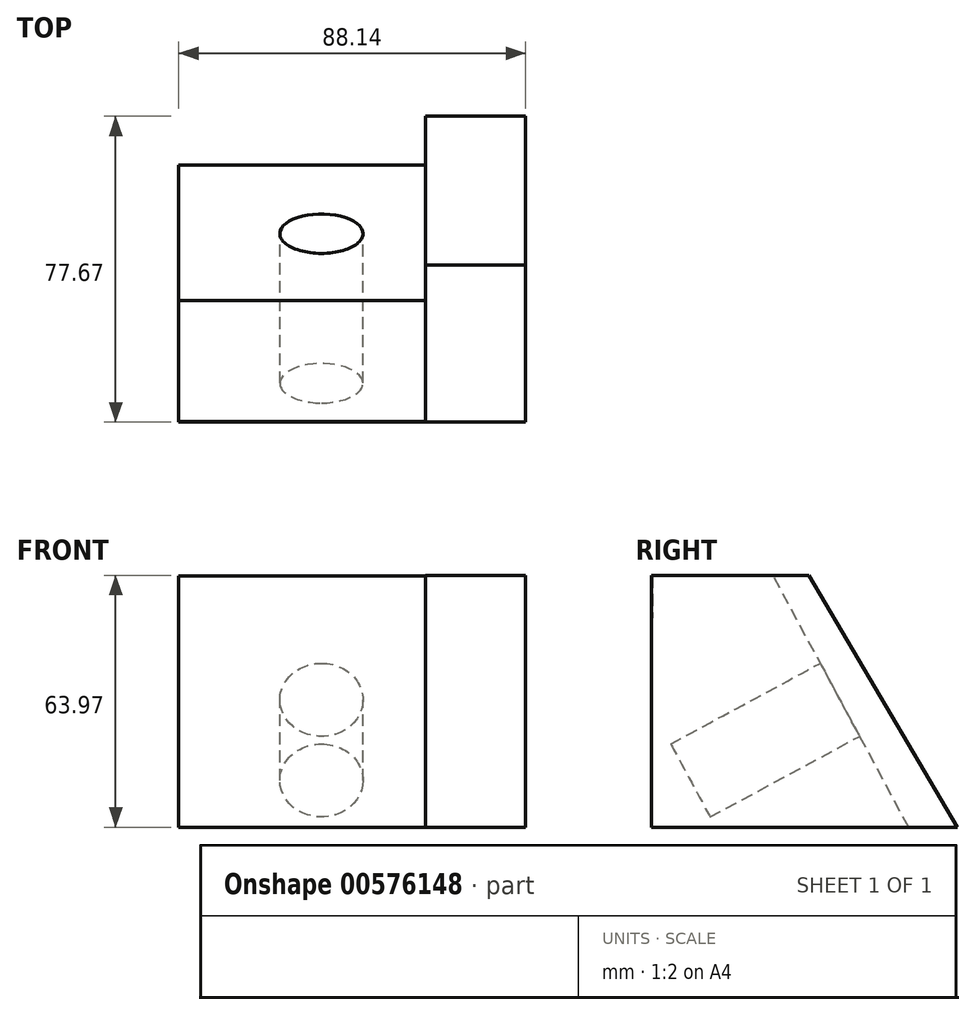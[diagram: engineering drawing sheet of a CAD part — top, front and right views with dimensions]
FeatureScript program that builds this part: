
annotation { "Feature Type Name" : "Feature", "Feature Type Description" : "" }
export const myFeature = defineFeature(function(context is Context, id is Id, definition is map)
    precondition{}
    {
        {
            var Q0;
            Q0=qCreatedBy(makeId("Right.planeOp"),FACE);
            var sketch = newSketch(context, id + "F0", { "sketchPlane" : qUnion([Q0])});
            skLineSegment(sketch, "E0.bottom", {"start": v(0, 0) * mm, "end": v(-39.92, 0) * mm});
            skLineSegment(sketch, "E0.top", {"start": v(0, 63.97) * mm, "end": v(-39.92, 63.97) * mm});
            skLineSegment(sketch, "E0.left", {"start": v(0, 0) * mm, "end": v(0, 63.97) * mm});
            skLineSegment(sketch, "E0.right", {"start": v(-39.92, 0) * mm, "end": v(-39.92, 63.97) * mm});
            skLineSegment(sketch, "E1", {"start": v(0, 63.97) * mm, "end": v(37.75, 0) * mm});
            skLineSegment(sketch, "E2", {"start": v(37.75, 0) * mm, "end": v(0, 0) * mm});
            skSolve(sketch);
        }
        {
            var Q0;
            Q0 = qSketchRegion(id + "F0", true);
            extrude(context, id + "F1", {"entities" : qUnion([Q0]), "depth" : 25.4 * mm, "offsetDistance" : 25.4 * mm});
        }
        {
            var Q0;
            Q0=qCreatedBy(makeId("Right.planeOp"),FACE);
            var sketch = newSketch(context, id + "F2", { "sketchPlane" : qUnion([Q0])});
            skLineSegment(sketch, "E3", {"start": v(-39.92, 0) * mm, "end": v(25.39, 0) * mm});
            skLineSegment(sketch, "E4", {"start": v(25.39, 0) * mm, "end": v(-9.02, 63.8) * mm});
            skLineSegment(sketch, "E5", {"start": v(-9.02, 63.8) * mm, "end": v(-39.75, 63.8) * mm});
            skLineSegment(sketch, "E6", {"start": v(-39.75, 63.8) * mm, "end": v(-39.92, 0) * mm});
            skSolve(sketch);
        }
        {
            var Q0;
            Q0 = qSketchRegion(id + "F2", true);
            extrude(context, id + "F3", {"entities" : qUnion([Q0]), "operationType" : NewBodyOperationType.ADD, "oppositeDirection" : true, "depth" : 62.74 * mm, "offsetDistance" : 25.4 * mm});
        }
        {
            var Q0;
            Q0=makeQuery(id+"F3.opExtrude","SWEPT_FACE",FACE,{"disambiguationData":[OSD([sQuery(id+"F2.wireOp",EDGE,"E4")])]});
            var sketch = newSketch(context, id + "F4", { "sketchPlane" : qUnion([Q0])});
            skCircle(sketch, "E7", {"center": v(26.51, 24.74) * mm, "radius": 10.55 * mm});
            skSolve(sketch);
        }
        {
            var Q0;
            Q0 = qSketchRegion(id + "F4", true);
            extrude(context, id + "F5", {"entities" : qUnion([Q0]), "operationType" : NewBodyOperationType.REMOVE, "oppositeDirection" : true, "depth" : 43.18 * mm, "offsetDistance" : 25.4 * mm});
        }
    });
